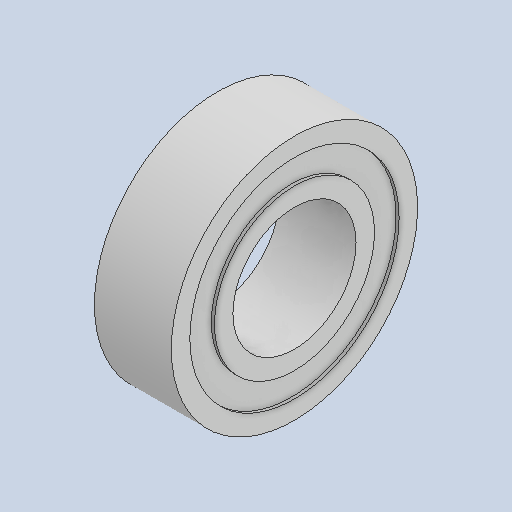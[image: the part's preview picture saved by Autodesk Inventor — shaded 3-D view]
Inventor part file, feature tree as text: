
AUTODESK INVENTOR PART (.ipt)
format: ipt  version: 2022.3 (Build 263350000, 350)  size: 123,904 bytes
history: native  units: in
note: dims shown in document units (in); Inventor stores cm internally (conversion verified against a paired STEP export)
features: revolve x1
ambient origin geometry x8: Origin, YZ Plane, XZ Plane, XY Plane, X Axis, Y Axis, Z Axis, Center Point
bodies: Solid1 (feature_tree)
feature tree (1):
  revolve  "Revolve1"  [1 undecoded]
note: 1 required parameter value undecoded (feature->parameter linkage not recoverable at this tier; creation-order binding heuristic only, values carry confidence <= 0.55)
